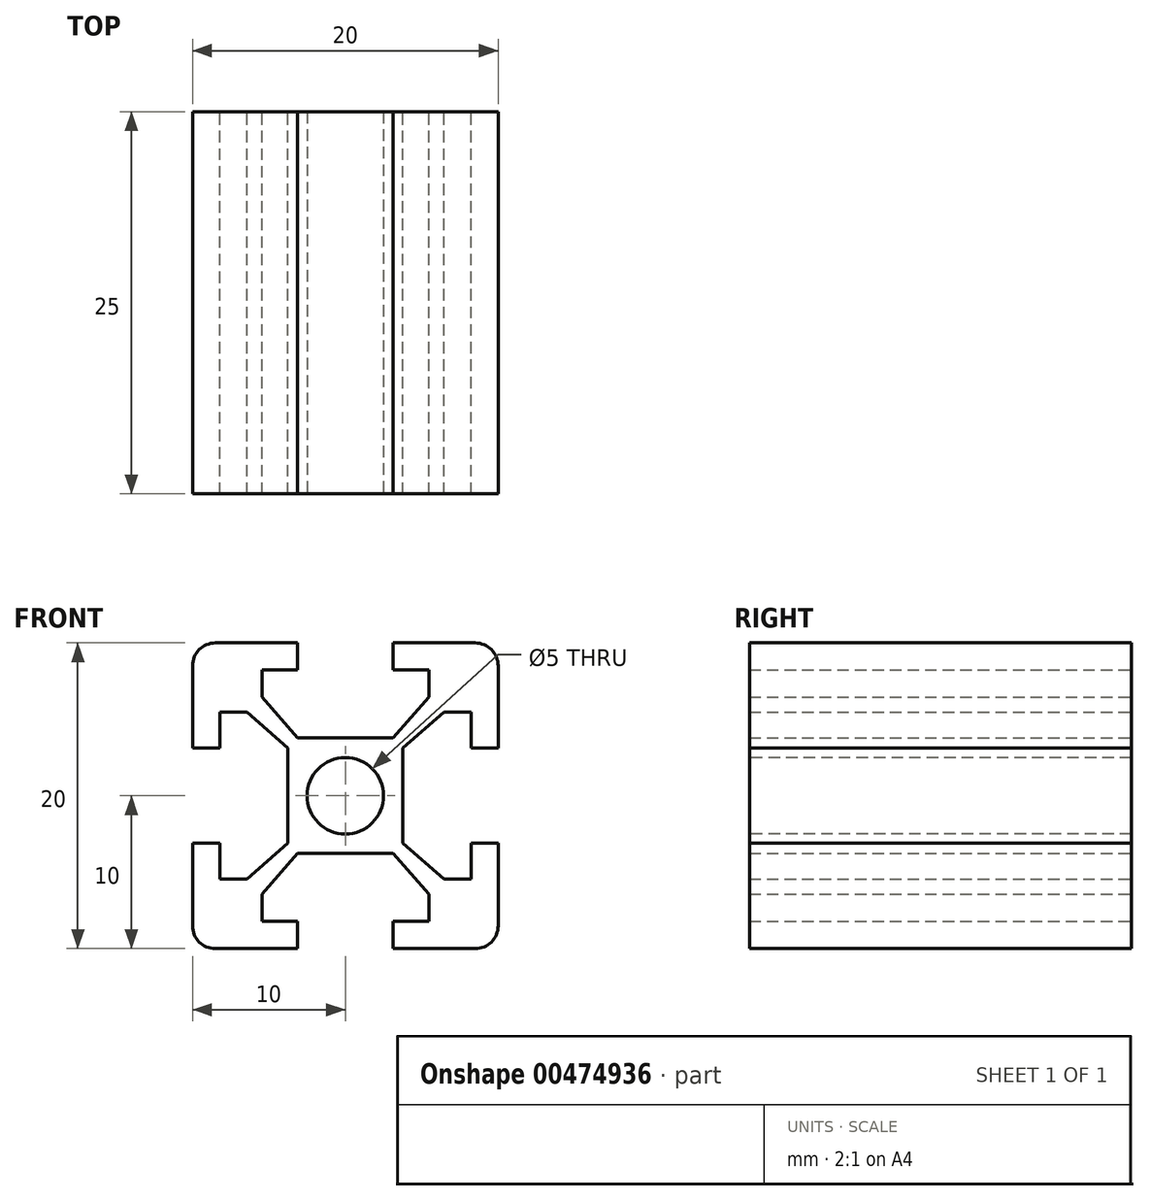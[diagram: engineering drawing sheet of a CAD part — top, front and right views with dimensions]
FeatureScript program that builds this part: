
annotation { "Feature Type Name" : "Feature", "Feature Type Description" : "" }
export const myFeature = defineFeature(function(context is Context, id is Id, definition is map)
    precondition{}
    {
        {
            var Q0;
            Q0=qCreatedBy(makeId("Front.planeOp"),FACE);
            var sketch = newSketch(context, id + "F0", { "sketchPlane" : qUnion([Q0])});
            skLineSegment(sketch, "E0.bottom", {"start": v(10, 10) * mm, "end": v(-10, 10) * mm});
            skLineSegment(sketch, "E0.top", {"start": v(10, -10) * mm, "end": v(-10, -10) * mm});
            skLineSegment(sketch, "E0.left", {"start": v(10, 10) * mm, "end": v(10, -10) * mm});
            skLineSegment(sketch, "E0.right", {"start": v(-10, 10) * mm, "end": v(-10, -10) * mm});
            skPoint(sketch, "E0.middle", {"position": v(0, 0) * mm});
            skLineSegment(sketch, "E1", {"start": v(3.11, 10) * mm, "end": v(3.11, 8.22) * mm});
            skLineSegment(sketch, "E2", {"start": v(3.11, 8.22) * mm, "end": v(5.46, 8.22) * mm});
            skLineSegment(sketch, "E3", {"start": v(5.46, 8.22) * mm, "end": v(5.46, 6.44) * mm});
            skLineSegment(sketch, "E4", {"start": v(5.46, 6.44) * mm, "end": v(3.11, 3.78) * mm});
            skLineSegment(sketch, "E5", {"start": v(3.11, 3.78) * mm, "end": v(0, 3.78) * mm});
            skLineSegment(sketch, "E6.MirrorCS", {"start": v(-3.11, 3.78) * mm, "end": v(0, 3.78) * mm});
            skLineSegment(sketch, "E7.MirrorCS", {"start": v(-5.46, 6.44) * mm, "end": v(-3.11, 3.78) * mm});
            skLineSegment(sketch, "E8.MirrorCS", {"start": v(-3.11, 10) * mm, "end": v(-3.11, 8.22) * mm});
            skLineSegment(sketch, "E9.MirrorCS", {"start": v(-5.46, 8.22) * mm, "end": v(-5.46, 6.44) * mm});
            skLineSegment(sketch, "E10.MirrorCS", {"start": v(-3.11, 8.22) * mm, "end": v(-5.46, 8.22) * mm});
            skLineSegment(sketch, "E11.1.0", {"start": v(-10, 3.11) * mm, "end": v(-8.22, 3.11) * mm});
            skLineSegment(sketch, "E11.1.1", {"start": v(-8.22, 3.11) * mm, "end": v(-8.22, 5.46) * mm});
            skLineSegment(sketch, "E11.1.2", {"start": v(-8.22, 5.46) * mm, "end": v(-6.44, 5.46) * mm});
            skLineSegment(sketch, "E11.1.3", {"start": v(-6.44, 5.46) * mm, "end": v(-3.78, 3.11) * mm});
            skLineSegment(sketch, "E11.1.4", {"start": v(-3.78, 3.11) * mm, "end": v(-3.78, 0) * mm});
            skLineSegment(sketch, "E11.1.5", {"start": v(-3.78, -3.11) * mm, "end": v(-3.78, 0) * mm});
            skLineSegment(sketch, "E11.1.6", {"start": v(-6.44, -5.46) * mm, "end": v(-3.78, -3.11) * mm});
            skLineSegment(sketch, "E11.1.7", {"start": v(-10, -3.11) * mm, "end": v(-8.22, -3.11) * mm});
            skLineSegment(sketch, "E11.1.8", {"start": v(-8.22, -5.46) * mm, "end": v(-6.44, -5.46) * mm});
            skLineSegment(sketch, "E11.1.9", {"start": v(-8.22, -3.11) * mm, "end": v(-8.22, -5.46) * mm});
            skLineSegment(sketch, "E11.2.0", {"start": v(-3.11, -10) * mm, "end": v(-3.11, -8.22) * mm});
            skLineSegment(sketch, "E11.2.1", {"start": v(-3.11, -8.22) * mm, "end": v(-5.46, -8.22) * mm});
            skLineSegment(sketch, "E11.2.2", {"start": v(-5.46, -8.22) * mm, "end": v(-5.46, -6.44) * mm});
            skLineSegment(sketch, "E11.2.3", {"start": v(-5.46, -6.44) * mm, "end": v(-3.11, -3.78) * mm});
            skLineSegment(sketch, "E11.2.4", {"start": v(-3.11, -3.78) * mm, "end": v(0, -3.78) * mm});
            skLineSegment(sketch, "E11.2.5", {"start": v(3.11, -3.78) * mm, "end": v(0, -3.78) * mm});
            skLineSegment(sketch, "E11.2.6", {"start": v(5.46, -6.44) * mm, "end": v(3.11, -3.78) * mm});
            skLineSegment(sketch, "E11.2.7", {"start": v(3.11, -10) * mm, "end": v(3.11, -8.22) * mm});
            skLineSegment(sketch, "E11.2.8", {"start": v(5.46, -8.22) * mm, "end": v(5.46, -6.44) * mm});
            skLineSegment(sketch, "E11.2.9", {"start": v(3.11, -8.22) * mm, "end": v(5.46, -8.22) * mm});
            skLineSegment(sketch, "E11.3.0", {"start": v(10, -3.11) * mm, "end": v(8.22, -3.11) * mm});
            skLineSegment(sketch, "E11.3.1", {"start": v(8.22, -3.11) * mm, "end": v(8.22, -5.46) * mm});
            skLineSegment(sketch, "E11.3.2", {"start": v(8.22, -5.46) * mm, "end": v(6.44, -5.46) * mm});
            skLineSegment(sketch, "E11.3.3", {"start": v(6.44, -5.46) * mm, "end": v(3.78, -3.11) * mm});
            skLineSegment(sketch, "E11.3.4", {"start": v(3.78, -3.11) * mm, "end": v(3.78, 0) * mm});
            skLineSegment(sketch, "E11.3.5", {"start": v(3.78, 3.11) * mm, "end": v(3.78, 0) * mm});
            skLineSegment(sketch, "E11.3.6", {"start": v(6.44, 5.46) * mm, "end": v(3.78, 3.11) * mm});
            skLineSegment(sketch, "E11.3.7", {"start": v(10, 3.11) * mm, "end": v(8.22, 3.11) * mm});
            skLineSegment(sketch, "E11.3.8", {"start": v(8.22, 5.46) * mm, "end": v(6.44, 5.46) * mm});
            skLineSegment(sketch, "E11.3.9", {"start": v(8.22, 3.11) * mm, "end": v(8.22, 5.46) * mm});
            skSolve(sketch);
        }
        {
            var Q0;
            {var subQ12=sQuery(id+"F0.wireOp",EDGE,"E1");Q0=makeQuery(id+"F0.imprint","IMPRINT",FACE,{"disambiguationData":[TD([[makeQuery(id+"F0.imprint","IMPRINT",EDGE,{"derivedFrom":subQ12}),1.0]])]});}
            extrude(context, id + "F1", {"entities" : qUnion([Q0]), "depth" : 25 * mm});
        }
        {
            var Q0;
            Q0=makeQuery(id+"F1.opExtrude","SWEPT_EDGE",EDGE,{"disambiguationData":[OSD([sQuery(id+"F0.wireOp",EDGE,"E0.bottom"),sQuery(id+"F0.wireOp",EDGE,"E0.right")])]});
            var Q1;
            Q1=makeQuery(id+"F1.opExtrude","SWEPT_EDGE",EDGE,{"disambiguationData":[OSD([sQuery(id+"F0.wireOp",EDGE,"E0.bottom"),sQuery(id+"F0.wireOp",EDGE,"E0.left")])]});
            var Q2;
            Q2=makeQuery(id+"F1.opExtrude","SWEPT_EDGE",EDGE,{"disambiguationData":[OSD([sQuery(id+"F0.wireOp",EDGE,"E0.top"),sQuery(id+"F0.wireOp",EDGE,"E0.left")])]});
            var Q3;
            Q3=makeQuery(id+"F1.opExtrude","SWEPT_EDGE",EDGE,{"disambiguationData":[OSD([sQuery(id+"F0.wireOp",EDGE,"E0.top"),sQuery(id+"F0.wireOp",EDGE,"E0.right")])]});
            fillet(context, id + "F2", {"entities" : qUnion([Q0, Q1, Q2, Q3]), "radius" : 1.5 * mm, "tangentPropagation" : true, "allowEdgeOverflow" : false});
        }
        {
            var Q0;
            Q0=makeQuery(id+"F1.opExtrude","CAP_FACE",FACE,{"disambiguationData":[OSD([sQuery(id+"F0.wireOp",EDGE,"E0.bottom"),sQuery(id+"F0.wireOp",EDGE,"E0.top"),sQuery(id+"F0.wireOp",EDGE,"E0.left"),sQuery(id+"F0.wireOp",EDGE,"E0.right"),sQuery(id+"F0.wireOp",EDGE,"E1"),sQuery(id+"F0.wireOp",EDGE,"E2"),sQuery(id+"F0.wireOp",EDGE,"E3"),sQuery(id+"F0.wireOp",EDGE,"E4"),sQuery(id+"F0.wireOp",EDGE,"E5"),sQuery(id+"F0.wireOp",EDGE,"E6.MirrorCS"),sQuery(id+"F0.wireOp",EDGE,"E7.MirrorCS"),sQuery(id+"F0.wireOp",EDGE,"E8.MirrorCS"),sQuery(id+"F0.wireOp",EDGE,"E9.MirrorCS"),sQuery(id+"F0.wireOp",EDGE,"E10.MirrorCS"),sQuery(id+"F0.wireOp",EDGE,"E11.1.0"),sQuery(id+"F0.wireOp",EDGE,"E11.1.1"),sQuery(id+"F0.wireOp",EDGE,"E11.1.2"),sQuery(id+"F0.wireOp",EDGE,"E11.1.3"),sQuery(id+"F0.wireOp",EDGE,"E11.1.4"),sQuery(id+"F0.wireOp",EDGE,"E11.1.5"),sQuery(id+"F0.wireOp",EDGE,"E11.1.6"),sQuery(id+"F0.wireOp",EDGE,"E11.1.7"),sQuery(id+"F0.wireOp",EDGE,"E11.1.8"),sQuery(id+"F0.wireOp",EDGE,"E11.1.9"),sQuery(id+"F0.wireOp",EDGE,"E11.2.0"),sQuery(id+"F0.wireOp",EDGE,"E11.2.1"),sQuery(id+"F0.wireOp",EDGE,"E11.2.2"),sQuery(id+"F0.wireOp",EDGE,"E11.2.3"),sQuery(id+"F0.wireOp",EDGE,"E11.2.4"),sQuery(id+"F0.wireOp",EDGE,"E11.2.5"),sQuery(id+"F0.wireOp",EDGE,"E11.2.6"),sQuery(id+"F0.wireOp",EDGE,"E11.2.7"),sQuery(id+"F0.wireOp",EDGE,"E11.2.8"),sQuery(id+"F0.wireOp",EDGE,"E11.2.9"),sQuery(id+"F0.wireOp",EDGE,"E11.3.0"),sQuery(id+"F0.wireOp",EDGE,"E11.3.1"),sQuery(id+"F0.wireOp",EDGE,"E11.3.2"),sQuery(id+"F0.wireOp",EDGE,"E11.3.3"),sQuery(id+"F0.wireOp",EDGE,"E11.3.4"),sQuery(id+"F0.wireOp",EDGE,"E11.3.5"),sQuery(id+"F0.wireOp",EDGE,"E11.3.6"),sQuery(id+"F0.wireOp",EDGE,"E11.3.7"),sQuery(id+"F0.wireOp",EDGE,"E11.3.8"),sQuery(id+"F0.wireOp",EDGE,"E11.3.9")])],"isStart":false});
            var sketch = newSketch(context, id + "F3", { "sketchPlane" : qUnion([Q0])});
            skCircle(sketch, "E12", {"center": v(0, 0) * mm, "radius": 2.5 * mm});
            skSolve(sketch);
        }
        {
            var Q0;
            Q0=qSketchRegion(id+"F3",true);
            var Q1;
            Q1=makeQuery(id+"F1.opExtrude","CAP_FACE",FACE,{"disambiguationData":[OSD([sQuery(id+"F0.wireOp",EDGE,"E0.bottom"),sQuery(id+"F0.wireOp",EDGE,"E0.top"),sQuery(id+"F0.wireOp",EDGE,"E0.left"),sQuery(id+"F0.wireOp",EDGE,"E0.right"),sQuery(id+"F0.wireOp",EDGE,"E1"),sQuery(id+"F0.wireOp",EDGE,"E2"),sQuery(id+"F0.wireOp",EDGE,"E3"),sQuery(id+"F0.wireOp",EDGE,"E4"),sQuery(id+"F0.wireOp",EDGE,"E5"),sQuery(id+"F0.wireOp",EDGE,"E6.MirrorCS"),sQuery(id+"F0.wireOp",EDGE,"E7.MirrorCS"),sQuery(id+"F0.wireOp",EDGE,"E8.MirrorCS"),sQuery(id+"F0.wireOp",EDGE,"E9.MirrorCS"),sQuery(id+"F0.wireOp",EDGE,"E10.MirrorCS"),sQuery(id+"F0.wireOp",EDGE,"E11.1.0"),sQuery(id+"F0.wireOp",EDGE,"E11.1.1"),sQuery(id+"F0.wireOp",EDGE,"E11.1.2"),sQuery(id+"F0.wireOp",EDGE,"E11.1.3"),sQuery(id+"F0.wireOp",EDGE,"E11.1.4"),sQuery(id+"F0.wireOp",EDGE,"E11.1.5"),sQuery(id+"F0.wireOp",EDGE,"E11.1.6"),sQuery(id+"F0.wireOp",EDGE,"E11.1.7"),sQuery(id+"F0.wireOp",EDGE,"E11.1.8"),sQuery(id+"F0.wireOp",EDGE,"E11.1.9"),sQuery(id+"F0.wireOp",EDGE,"E11.2.0"),sQuery(id+"F0.wireOp",EDGE,"E11.2.1"),sQuery(id+"F0.wireOp",EDGE,"E11.2.2"),sQuery(id+"F0.wireOp",EDGE,"E11.2.3"),sQuery(id+"F0.wireOp",EDGE,"E11.2.4"),sQuery(id+"F0.wireOp",EDGE,"E11.2.5"),sQuery(id+"F0.wireOp",EDGE,"E11.2.6"),sQuery(id+"F0.wireOp",EDGE,"E11.2.7"),sQuery(id+"F0.wireOp",EDGE,"E11.2.8"),sQuery(id+"F0.wireOp",EDGE,"E11.2.9"),sQuery(id+"F0.wireOp",EDGE,"E11.3.0"),sQuery(id+"F0.wireOp",EDGE,"E11.3.1"),sQuery(id+"F0.wireOp",EDGE,"E11.3.2"),sQuery(id+"F0.wireOp",EDGE,"E11.3.3"),sQuery(id+"F0.wireOp",EDGE,"E11.3.4"),sQuery(id+"F0.wireOp",EDGE,"E11.3.5"),sQuery(id+"F0.wireOp",EDGE,"E11.3.6"),sQuery(id+"F0.wireOp",EDGE,"E11.3.7"),sQuery(id+"F0.wireOp",EDGE,"E11.3.8"),sQuery(id+"F0.wireOp",EDGE,"E11.3.9")])],"isStart":true});
            extrude(context, id + "F4", {"entities" : qUnion([Q0]), "operationType" : NewBodyOperationType.REMOVE, "endBound" : BoundingType.UP_TO_SURFACE, "oppositeDirection" : true, "endBoundEntityFace" : qUnion([Q1]), "depth" : 25 * mm});
        }
    });
